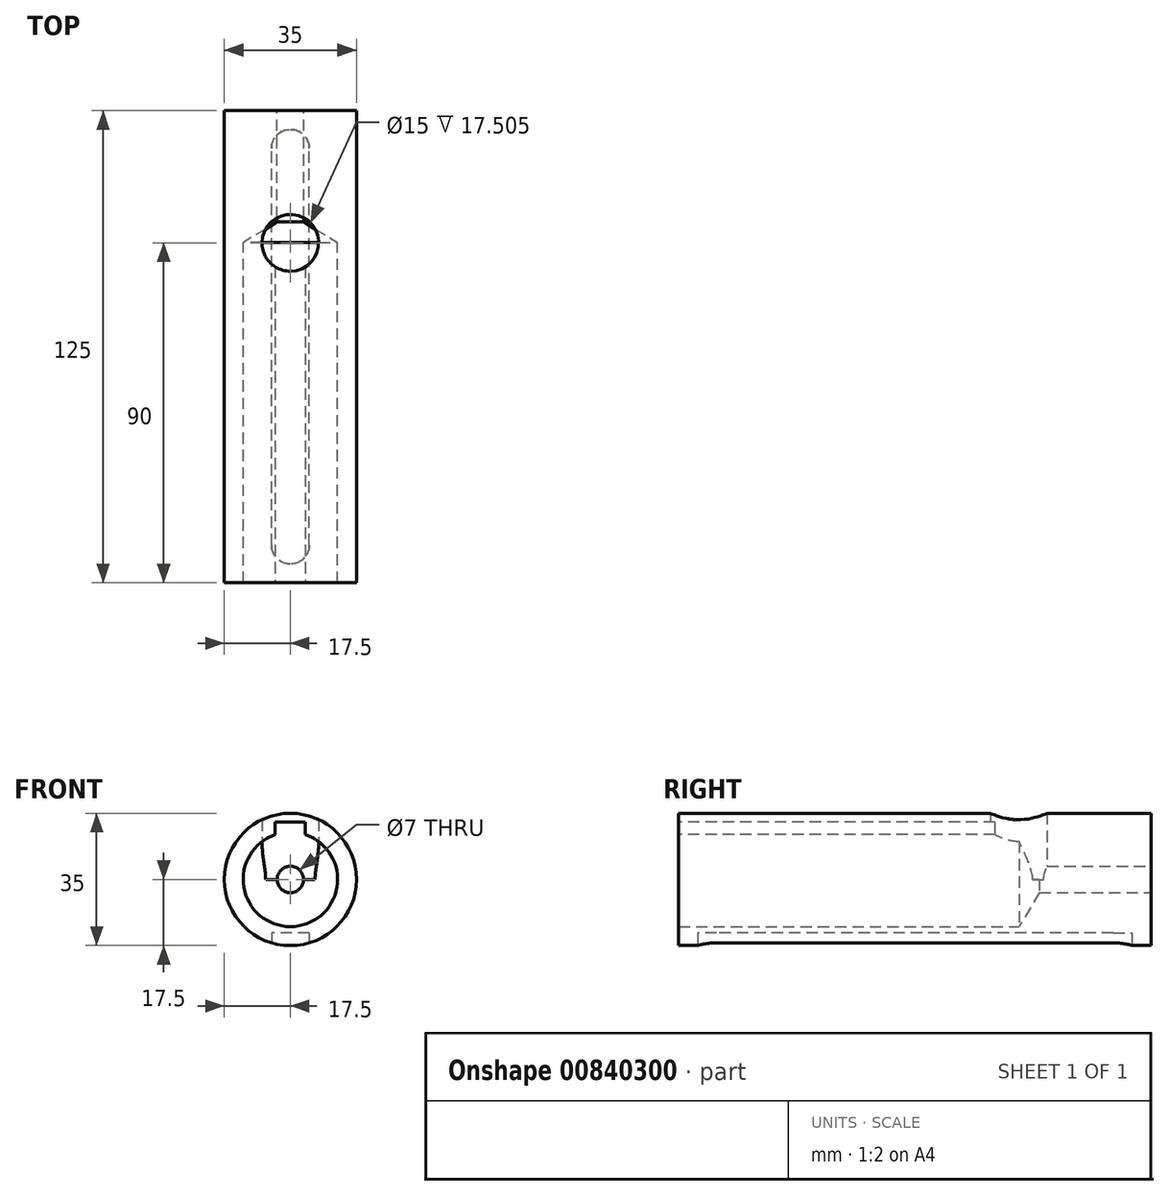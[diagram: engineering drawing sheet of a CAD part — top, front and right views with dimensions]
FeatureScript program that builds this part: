
annotation { "Feature Type Name" : "Feature", "Feature Type Description" : "" }
export const myFeature = defineFeature(function(context is Context, id is Id, definition is map)
    precondition{}
    {
        {
            var Q0;
            Q0=qCreatedBy(makeId("Front.planeOp"),FACE);
            var sketch = newSketch(context, id + "F0", { "sketchPlane" : qUnion([Q0])});
            skCircle(sketch, "E0", {"center": v(0, 0) * mm, "radius": 17.5 * mm});
            skCircle(sketch, "E1", {"center": v(0, 0) * mm, "radius": 12.5 * mm});
            skSolve(sketch);
        }
        {
            var Q0;
            Q0 = qSketchRegion(id + "F0", true);
            extrude(context, id + "F1", {"entities" : qUnion([Q0]), "endBound" : BoundingType.SYMMETRIC, "depth" : 90 * mm, "offsetDistance" : 25 * mm});
        }
        {
            var Q0;
            Q0=makeQuery(id+"F1.opExtrude","CAP_FACE",FACE,{"disambiguationData":[OSD([sQuery(id+"F0.wireOp",EDGE,"E0"),sQuery(id+"F0.wireOp",EDGE,"E1")])],"isStart":false});
            var sketch = newSketch(context, id + "F2", { "sketchPlane" : qUnion([Q0])});
            skLineSegment(sketch, "E2.bottom", {"start": v(-4, 11.84) * mm, "end": v(4, 11.84) * mm});
            skLineSegment(sketch, "E2.top", {"start": v(-4, 15.14) * mm, "end": v(4, 15.14) * mm});
            skLineSegment(sketch, "E2.left", {"start": v(-4, 11.84) * mm, "end": v(-4, 15.14) * mm});
            skLineSegment(sketch, "E2.right", {"start": v(4, 11.84) * mm, "end": v(4, 15.14) * mm});
            skLineSegment(sketch, "E3", {"start": v(0, 11.84) * mm, "end": v(0, 0) * mm, "construction": true});
            skSolve(sketch);
        }
        {
            var Q0;
            Q0 = qSketchRegion(id + "F2", true);
            extrude(context, id + "F3", {"entities" : qUnion([Q0]), "operationType" : NewBodyOperationType.REMOVE, "endBound" : BoundingType.THROUGH_ALL, "oppositeDirection" : true, "depth" : 25 * mm, "offsetDistance" : 25 * mm});
        }
        {
            var Q0;
            Q0=makeQuery(id+"F1.opExtrude","CAP_FACE",FACE,{"disambiguationData":[OSD([sQuery(id+"F0.wireOp",EDGE,"E0"),sQuery(id+"F0.wireOp",EDGE,"E1")])],"isStart":true});
            var sketch = newSketch(context, id + "F4", { "sketchPlane" : qUnion([Q0])});
            skCircle(sketch, "E4", {"center": v(0, 0) * mm, "radius": 17.5 * mm});
            skSolve(sketch);
        }
        {
            var Q0;
            Q0 = qSketchRegion(id + "F4", true);
            extrude(context, id + "F5", {"entities" : qUnion([Q0]), "operationType" : NewBodyOperationType.ADD, "depth" : 35 * mm, "offsetDistance" : 25 * mm});
        }
        {
            var Q0;
            Q0=qCreatedBy(makeId("Top.planeOp"),FACE);
            cPlane(context, id + "F6", {"entities" : qUnion([Q0]), "cplaneType" : CPlaneType.OFFSET, "offset" : 17.5 * mm, "oppositeDirection" : true, "width" : 150 * mm, "height" : 150 * mm});
        }
        {
            var Q0;
            Q0=qCreatedBy(id+"F6.planeOp",FACE);
            var sketch = newSketch(context, id + "F7", { "sketchPlane" : qUnion([Q0])});
            skLineSegment(sketch, "E5", {"start": v(0, 70) * mm, "end": v(0, -35) * mm});
            skArc(sketch, "E6.0.startCap", {"start": v(-5, 70) * mm, "mid": v(0, 75) * mm, "end": v(5, 70) * mm});
            skArc(sketch, "E6.0.endCap", {"start": v(5, -35) * mm, "mid": v(0, -40) * mm, "end": v(-5, -35) * mm});
            skLineSegment(sketch, "E6.0.left", {"start": v(5, 70) * mm, "end": v(5, -35) * mm});
            skLineSegment(sketch, "E6.0.right", {"start": v(-5, 70) * mm, "end": v(-5, -35) * mm});
            skSolve(sketch);
        }
        {
            var Q0;
            Q0 = qSketchRegion(id + "F7", true);
            extrude(context, id + "F8", {"entities" : qUnion([Q0]), "operationType" : NewBodyOperationType.REMOVE, "depth" : 3.3 * mm, "offsetDistance" : 25 * mm});
        }
        {
            var Q0;
            Q0=qCreatedBy(makeId("Top.planeOp"),FACE);
            var sketch = newSketch(context, id + "F9", { "sketchPlane" : qUnion([Q0])});
            skCircle(sketch, "E7", {"center": v(0, 45) * mm, "radius": 7.5 * mm});
            skSolve(sketch);
        }
        {
            var Q0;
            Q0 = qSketchRegion(id + "F9", true);
            extrude(context, id + "F10", {"entities" : qUnion([Q0]), "operationType" : NewBodyOperationType.REMOVE, "depth" : 25 * mm, "offsetDistance" : 25 * mm});
        }
        {
            var Q0;
            Q0=makeQuery(id+"F5.opExtrude","CAP_FACE",FACE,{"disambiguationData":[OSD([sQuery(id+"F4.wireOp",EDGE,"E4")])],"isStart":true});
            var sketch = newSketch(context, id + "F11", { "sketchPlane" : qUnion([Q0])});
            skPoint(sketch, "E8", {"position": v(0, 0) * mm});
            skSolve(sketch);
        }
        {
            var Q0;
            Q0=sQuery(id+"F11.wireOp",VERTEX,"E8");
            var Q1;
            Q1=makeQuery(id+"F1.opExtrude","SWEPT_BODY",BODY,{"disambiguationData":[OSD([sQuery(id+"F0.wireOp",EDGE,"E0"),sQuery(id+"F0.wireOp",EDGE,"E1")])]});
            hole(context, id + "F12", {"style" : HoleStyle.SIMPLE, "endStyle" : HoleEndStyle.BLIND, "standardTappedOrClearance" : lookupTablePath({ "standard" : "ISO", "size" : "25", "type" : "Drilled" }), "standardBlindInLast" : lookupTablePath({ "standard" : "ISO", "size" : "25", "type" : "Drilled" }), "holeDiameter" : 25 * mm, "majorDiameter" : 5 * mm, "holeDepth" : 0.1 * mm, "isTappedThrough" : true, "tappedDepth" : 12 * mm, "tapClearance" : 3, "startFromSketch" : true, "locations" : qUnion([Q0]), "scope" : qUnion([Q1])});
        }
        {
            var Q0;
            Q0=makeQuery(id+"F5.opExtrude","CAP_FACE",FACE,{"disambiguationData":[OSD([sQuery(id+"F4.wireOp",EDGE,"E4")])],"isStart":false});
            var sketch = newSketch(context, id + "F13", { "sketchPlane" : qUnion([Q0])});
            skPoint(sketch, "E9", {"position": v(0, 0) * mm});
            skSolve(sketch);
        }
        {
            var Q0;
            Q0=sQuery(id+"F13.wireOp",VERTEX,"E9");
            var Q1;
            Q1=makeQuery(id+"F1.opExtrude","SWEPT_BODY",BODY,{"disambiguationData":[OSD([sQuery(id+"F0.wireOp",EDGE,"E0"),sQuery(id+"F0.wireOp",EDGE,"E1")])]});
            hole(context, id + "F14", {"style" : HoleStyle.SIMPLE, "endStyle" : HoleEndStyle.THROUGH, "standardTappedOrClearance" : lookupTablePath({ "standard" : "ISO", "size" : "7", "type" : "Drilled" }), "standardBlindInLast" : lookupTablePath({ "standard" : "ISO", "size" : "7", "type" : "Drilled" }), "holeDiameter" : 7 * mm, "majorDiameter" : 5 * mm, "isTappedThrough" : true, "tappedDepth" : 12 * mm, "tapClearance" : 3, "startFromSketch" : true, "locations" : qUnion([Q0]), "scope" : qUnion([Q1])});
        }
    });
